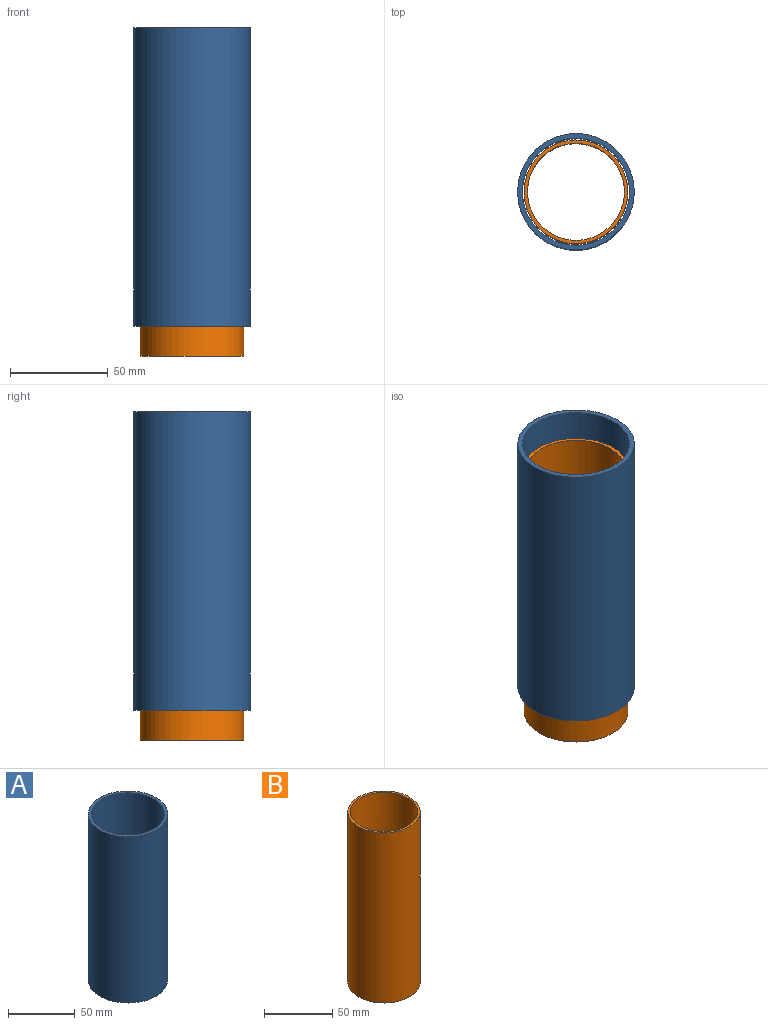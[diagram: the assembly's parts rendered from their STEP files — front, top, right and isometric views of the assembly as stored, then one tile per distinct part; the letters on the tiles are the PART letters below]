
ASSEMBLY  parts=2 mates=1
PART A: 4 faces, bbox 59.5x59.5x152.4 mm
  f0: cylinder r=29.75mm len=152.4mm, axis (0,0,-1), area 28486.8mm2, adj f1,f2
  f1: plane 59.5x59.5mm, normal (0,0,1), area 438.2mm2, adj f0,f3
  f2: plane 59.5x59.5mm, normal (0,0,-1), area 438.2mm2, adj f0,f3
  f3: cylinder r=27.3mm len=152.4mm, axis (0,0,1), area 26146.1mm2, adj f1,f2
PART B: 4 faces, bbox 53x53x152.4 mm
  f0: cylinder r=26.48mm len=152.4mm, axis (0,0,-1), area 25355.3mm2, adj f1,f2
  f1: plane 52.96x52.96mm, normal (0,0,1), area 276mm2, adj f0,f3
  f2: plane 52.96x52.96mm, normal (0,0,-1), area 276mm2, adj f0,f3
  f3: cylinder r=24.77mm len=152.4mm, axis (0,0,-1), area 23713.9mm2, adj f1,f2
PLACE A rot(axis=(0,0,-1),0deg) t=(82.09,-18.95,-156.12)mm fixed
PLACE B t=(82.09,-18.95,-324.02)mm
MATE slider B.f0 <-> A.f0  axis (0,0,-1) through (82.09,-18.95,-95.42)mm
